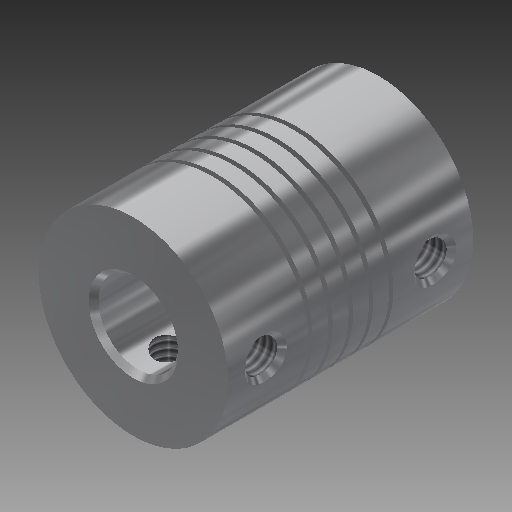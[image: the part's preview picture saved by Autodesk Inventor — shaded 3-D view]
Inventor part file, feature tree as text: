
AUTODESK INVENTOR PART (.ipt)
format: ipt  version: 2018 (Build 220112000, 112)  size: 356,864 bytes
history: native  units: in
note: dims shown in document units (in); Inventor stores cm internally (conversion verified against a paired STEP export)
features: sketch x5, extrude x2, hole x2, chamfer x2, helix x1, plane x1, other x1
ambient origin geometry x8: Origin, YZ Plane, XZ Plane, XY Plane, X Axis, Y Axis, Z Axis, Center Point
bodies: Solid1 (feature_tree)
feature tree (14):
  sketch  "Sketch1"  dims[d0=0.75in d1=0.1969in]
  extrude  "Extrusion1"  Depth=0.1969in
  extrude  "Extrusion2"  Depth=0.315in
  helix  "Coil1"  [1 undecoded]
  hole  "Hole1"  [1 undecoded]
  plane  "Work Plane2"
  hole  "Hole2"  [1 undecoded]
  chamfer  "Chamfer1"  Distance=0.1575in
  chamfer  "Chamfer2"  Distance=0.15in
  sketch  "Sketch3"  dims[d2=0.97in d3=0.0in d4=0.315in d5=0.69in d6=0.0in]
  sketch  "Sketch5"  dims[d8=0.017in]
  sketch  "Sketch6"  dims[d9=0.08in d10=1.0in d11=1.9685in d12=0.0in d13=90.0deg d14=90.0deg d15=0.0in d16=0.0in d17=0.277in]
  other  "Work Axis1"
  sketch  "Sketch8"  dims[d18=0.1575in d19=0.15in d20=0.1575in d21=0.15in d22=0.128in d23=0.75in d24=0.375in d25=0.25in d26=0.5635in d27=1.0in d28=0.8108in d29=90.0deg d30=0.1575in d31=0.1575in d32=0.15in d33=0.1496in d34=0.128in d35=0.75in d36=0.375in d37=0.25in d38=0.5635in d39=1.0in d40=0.8108in d41=0.0197in d42=0.125in d43=45.0deg d44=0.0197in d45=0.125in d46=45.0deg]
note: 3 required parameter values undecoded (feature->parameter linkage not recoverable at this tier; creation-order binding heuristic only, values carry confidence <= 0.55)
